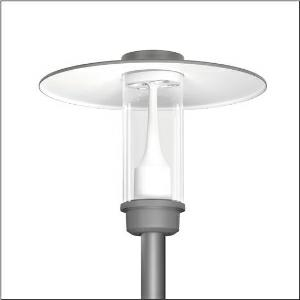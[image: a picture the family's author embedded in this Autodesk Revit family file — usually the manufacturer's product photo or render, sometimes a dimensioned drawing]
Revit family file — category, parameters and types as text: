
# Revit family: litepole_iq_2___p1_0a_5xa5425bf14h_bae2
name_source: partatom
category: Lighting Fixtures
units: mm (PartAtom-declared; Revit-internal decimal feet)

## family parameters
Cut with Voids When Loaded = No
Host = Face
Light Source = No
Part Type = Normal
Room Calculation Point = No
Round Connector Dimension = Use Diameter
Shared = No

## types (1)
- --- (1 x LED, 1520 lm, 12.9 W, 2200K)
    Apparent Load = 13 VA
    CIE Flux Codes = 33 62 89 96 100
    Color Rendering = 70
    Color Temperature = 2200K
    Default Elevation = 1800 mm
    Description = Litepole iQ 2, mast luminaire, Module 540 iQ-SR, primary light control with 3 zone facetted reflector, of plastic, silver coated, highly specular, structured, primary optical cover: cover, of PMMA, transparent, light distribution: P1.0a, light emission: direct distribution, primary light characteristic: strongly asymmetric, installation type: post-top, LED, High Power LED, rated luminous flux: 1.520lm, luminous efficacy: 118lm/W, light colour: 722, colour temperature: 2200K, control gear: ECG iQ, control: presetting dimming logarithmic, Street-Remote, Auto-Match, Temp-Guard, Lumen-Switch, Night-Set, Smart-Wire, Light-Fading, Desk-Remote (wireless, voltage-free reading and setting of iQ features in the workshop via application-optimized NFC function/RFID function), optimised constant luminous flux control (CLO 2.0), with terminal, 6-pole, max. 2.5mm², mains connection: 220..240V, AC, 50/60Hz, start of lifetime: 13W, end of lifetime: 13W, reduction: 6W, luminaire housing, upper part, of aluminium, coated, Siteco® metallic grey (DB 702S), diameter: 750mm, height: 590mm, spigot size: d x l = 76 x 70mm (post-top) | with reducer (optional accessory) 60 x 70mm, post-top mast mounting element, of diecast aluminium, coated, Siteco® metallic grey (DB 702S), Module 540 iQ-SR, traffic white (RAL 9016), equipment: standard, protection rating (complete): IP65, insulation class (complete): insulation class II (safety insulation), certification: CE, ENEC, VDE, packaging unit: 1 piece

Light Distribution: P1.0a
    Height = 590 mm
    Lamp = 1 x LED
    Lamp Light Flux = 1520 lm
    Lamp Power = 12.9 W
    Lamp count = 1
    Length = 750 mm
    Luminous efficacy = 118 lm/W
    Manufacturer = Siteco
    ModVariant = No
    Model = 5XA5425BF14H
    Number of Poles = 1
    OnlyDefault = Yes
    Power Factor = 1
    Product Name = Litepole iQ 2 | P1.0a
    Product group = mast luminaire | pylon top
    ProductGroupID = 6100
    Protection Class = Protection class II
    Protection Degree = IP 65
    RLX_Detail_Level = 1
    RlxData = <blob elided: 138853 chars, md5=2aa3b643>
    Socket = socket
    Standby Power = 0 W
    System Light Flux = 1520 lm
    System Power = 13 W
    Type Comments = factory setting: luminous flux: 100 % | dim-lin: 254 | 516 mA
    Type Image = l_1006518.jpg
    URL = http://relux.com
    VarID = @adj_112981
    Voltage = 0 V
    Weight = 0.00 kg
    Width = 0 mm  [stored 0 ft]

note: [stored X ft] marks values corroborated as IEEE doubles in the binary element streams (Revit-internal decimal feet)

## geometry (parser evidence)
native form markers: Blend x4, Sweep x11
no freeform markers — native parametric forms only
